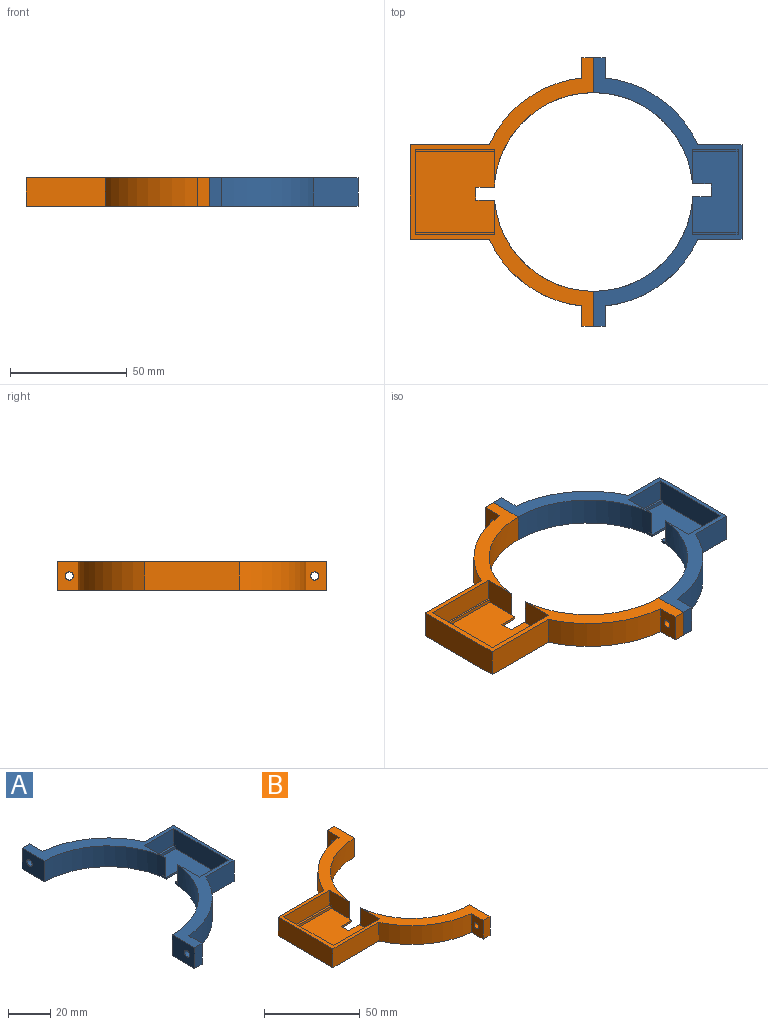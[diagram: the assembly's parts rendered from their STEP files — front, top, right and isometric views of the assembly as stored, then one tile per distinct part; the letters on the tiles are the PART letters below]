
ASSEMBLY  parts=2 mates=1
PART A: 30 faces, bbox 63.5x115x12 mm
  f0: cylinder r=42.5mm len=42.36mm, axis (0,0,1), area 752.2mm2, adj f1,f4,f10,f11,f20,f29
  f1: plane 115x63.5mm, normal (0,0,-1), area 1622mm2, adj f0,f6,f7,f8,f9,f10,f12,f13
  f2: plane 19.5x9.5mm, normal (0,1,0), area 185.3mm2, adj f3,f5,f11,f24
  f3: plane 14.13x11mm, normal (1,0,0), area 153.9mm2, adj f2,f4,f6,f11,f23,f24
  f4: plane 34.5x19.5mm, normal (0,0,1), area 628.2mm2, adj f0,f3,f5,f6,f20,f21,f23,f27
  f5: plane 36.5x11mm, normal (-1,0,0), area 398.5mm2, adj f2,f4,f11,f19,f21,f22,f23,f24
  f6: cylinder r=42.5mm len=42.45mm, axis (0,0,1), area 753.7mm2, adj f1,f3,f4,f8,f11,f27
  f7: cylinder r=49mm len=39.62mm, axis (0,0,1), area 613mm2, adj f1,f11,f12,f17
  f8: plane 15x12mm, normal (-1,0,0), area 170.4mm2, adj f1,f6,f11,f14,f25
  f9: cylinder r=49mm len=39.62mm, axis (0,0,1), area 613mm2, adj f1,f11,f15,f18
  f10: plane 15x12mm, normal (-1,0,0), area 170.4mm2, adj f0,f1,f11,f13,f26
  f11: plane 115x63.5mm, normal (0,0,1), area 954.7mm2, adj f0,f2,f3,f5,f6,f7,f8,f9
  f12: plane 12x8.76mm, normal (1,0,0), area 95.4mm2, adj f1,f7,f11,f13,f26
  f13: plane 12x5mm, normal (0,1,0), area 60mm2, adj f1,f10,f11,f12
  f14: plane 12x5mm, normal (0,-1,0), area 60mm2, adj f1,f8,f11,f15
  f15: plane 12x8.76mm, normal (1,0,0), area 95.4mm2, adj f1,f9,f11,f14,f25
  f16: plane 40.5x12mm, normal (1,0,0), area 486mm2, adj f1,f11,f17,f18
  f17: plane 18.88x12mm, normal (0,1,0), area 226.6mm2, adj f1,f7,f11,f16
  f18: plane 18.88x12mm, normal (0,-1,0), area 226.6mm2, adj f1,f9,f11,f16
  f19: plane 19.5x9.5mm, normal (0,-1,0), area 185.3mm2, adj f5,f11,f20,f22
  f20: plane 14.13x11mm, normal (1,0,0), area 153.9mm2, adj f0,f4,f11,f19,f21,f22
  f21: plane 19.5x1.5mm, normal (0,-1,0), area 29.3mm2, adj f4,f5,f20,f22
  f22: plane 19.5x1mm, normal (0,0,1), area 19.5mm2, adj f5,f19,f20,f21
  f23: plane 19.5x1.5mm, normal (0,1,0), area 29.3mm2, adj f3,f4,f5,f24
  f24: plane 19.5x1mm, normal (0,0,1), area 19.5mm2, adj f2,f3,f5,f23
  f25: cylinder r=1.75mm len=5mm, axis (1,0,0), area 55mm2, adj f8,f15
  f26: cylinder r=1.75mm len=5mm, axis (1,0,0), area 55mm2, adj f10,f12
  f27: plane 7.9x1mm, normal (0,1,0), area 7.9mm2, adj f1,f4,f6,f28
  f28: plane 5.5x1mm, normal (-1,0,0), area 5.5mm2, adj f1,f4,f27,f29
  f29: plane 8x1mm, normal (0,-1,0), area 8mm2, adj f0,f1,f4,f28
PART B: 30 faces, bbox 78.5x115x12 mm
  f0: cylinder r=42.5mm len=42.36mm, axis (0,0,1), area 752.2mm2, adj f1,f5,f7,f11,f20,f28
  f1: plane 34.5x34mm, normal (0,0,1), area 1128.8mm2, adj f0,f2,f4,f8,f20,f21,f23,f27
  f2: plane 36.5x11mm, normal (1,0,0), area 398.5mm2, adj f1,f3,f5,f19,f21,f22,f23,f24
  f3: plane 34x9.5mm, normal (0,1,0), area 323mm2, adj f2,f5,f20,f24
  f4: plane 14.13x11mm, normal (-1,0,0), area 153.9mm2, adj f1,f5,f8,f19,f21,f22
  f5: plane 115x78.5mm, normal (0,0,1), area 1033mm2, adj f0,f2,f3,f4,f6,f7,f8,f9
  f6: cylinder r=49mm len=39.62mm, axis (0,0,1), area 613mm2, adj f5,f11,f14,f16
  f7: plane 15x12mm, normal (1,0,0), area 170.4mm2, adj f0,f5,f11,f15,f25
  f8: cylinder r=42.5mm len=42.45mm, axis (0,0,1), area 753.7mm2, adj f1,f4,f5,f9,f11,f29
  f9: plane 15x12mm, normal (1,0,0), area 170.4mm2, adj f5,f8,f11,f12,f26
  f10: cylinder r=49mm len=39.62mm, axis (0,0,1), area 613mm2, adj f5,f11,f13,f17
  f11: plane 115x78.5mm, normal (0,0,-1), area 2229.8mm2, adj f0,f6,f7,f8,f9,f10,f12,f13
  f12: plane 12x5mm, normal (0,1,0), area 60mm2, adj f5,f9,f11,f13
  f13: plane 12x8.76mm, normal (-1,0,0), area 95.4mm2, adj f5,f10,f11,f12,f26
  f14: plane 12x8.76mm, normal (-1,0,0), area 95.4mm2, adj f5,f6,f11,f15,f25
  f15: plane 12x5mm, normal (0,-1,0), area 60mm2, adj f5,f7,f11,f14
  f16: plane 33.88x12mm, normal (0,-1,0), area 406.6mm2, adj f5,f6,f11,f18
  f17: plane 33.88x12mm, normal (0,1,0), area 406.6mm2, adj f5,f10,f11,f18
  f18: plane 40.5x12mm, normal (-1,0,0), area 486mm2, adj f5,f11,f16,f17
  f19: plane 34x9.5mm, normal (0,-1,0), area 323mm2, adj f2,f4,f5,f22
  f20: plane 14.13x11mm, normal (-1,0,0), area 153.9mm2, adj f0,f1,f3,f5,f23,f24
  f21: plane 34x1.5mm, normal (0,-1,0), area 51mm2, adj f1,f2,f4,f22
  f22: plane 34x1mm, normal (0,0,1), area 34mm2, adj f2,f4,f19,f21
  f23: plane 34x1.5mm, normal (0,1,0), area 51mm2, adj f1,f2,f20,f24
  f24: plane 34x1mm, normal (0,0,1), area 34mm2, adj f2,f3,f20,f23
  f25: cylinder r=1.75mm len=5mm, axis (-1,0,0), area 55mm2, adj f7,f14
  f26: cylinder r=1.75mm len=5mm, axis (-1,0,0), area 55mm2, adj f9,f13
  f27: plane 5.5x1mm, normal (1,0,0), area 5.5mm2, adj f1,f11,f28,f29
  f28: plane 7.94x1mm, normal (0,1,0), area 7.9mm2, adj f0,f1,f11,f27
  f29: plane 7.85x1mm, normal (0,-1,0), area 7.8mm2, adj f1,f8,f11,f27
PLACE A t=(-16.43,4.8,-12.07)mm
PLACE B t=(-16.43,4.8,-12.07)mm
MATE fastened B.f25 <-> A.f25  axis (1,0,0) through (-16.43,-47.7,-6.07)mm
